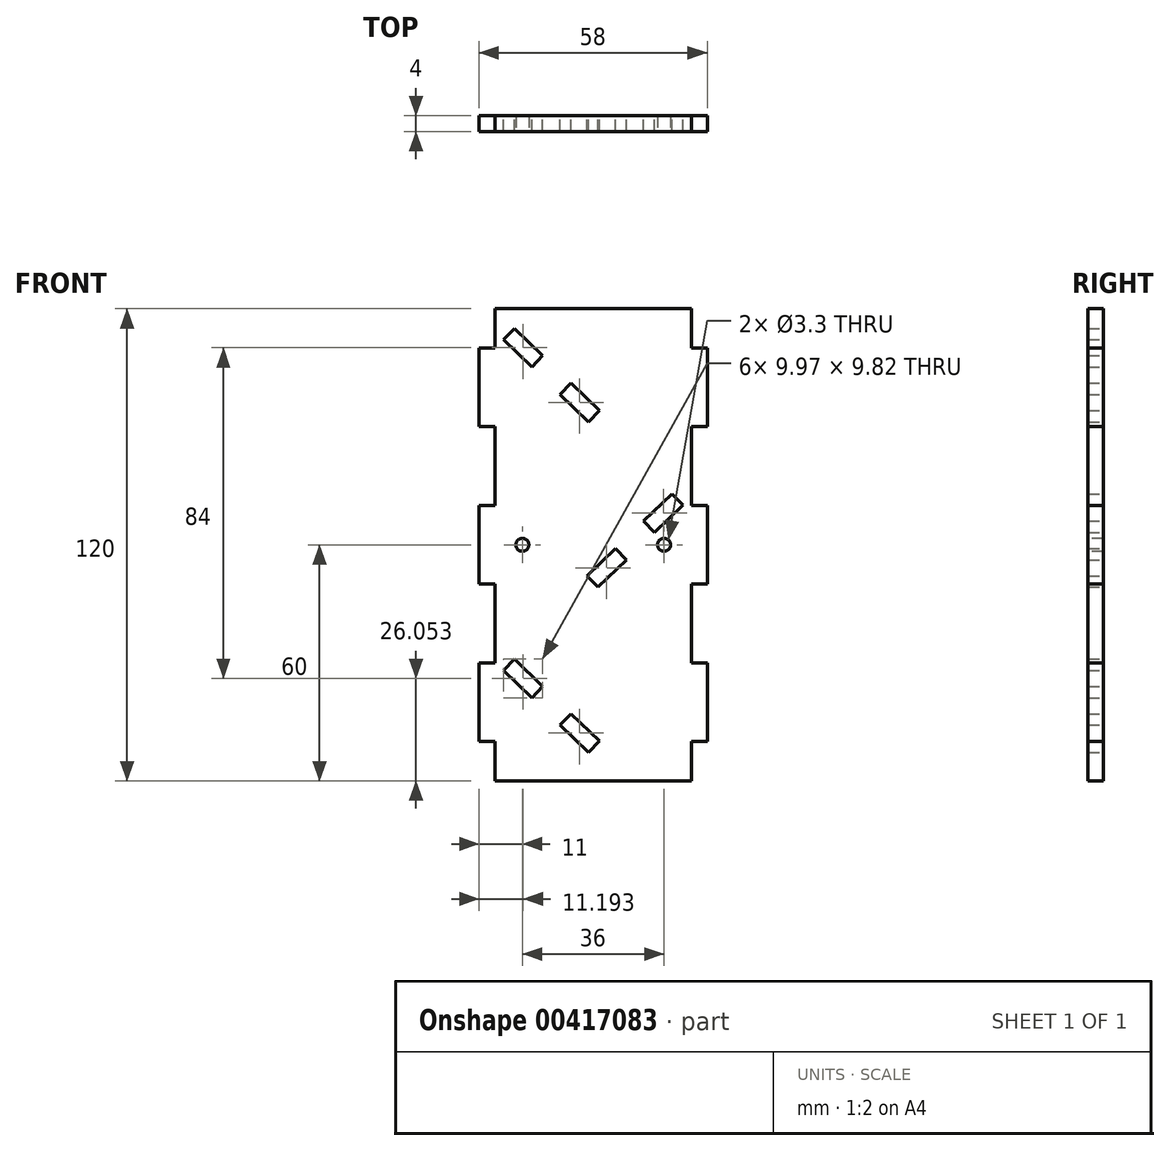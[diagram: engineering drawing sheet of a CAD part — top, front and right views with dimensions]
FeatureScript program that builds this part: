
annotation { "Feature Type Name" : "Feature", "Feature Type Description" : "" }
export const myFeature = defineFeature(function(context is Context, id is Id, definition is map)
    precondition{}
    {
        {
            var Q0;
            Q0=qCreatedBy(makeId("Front.planeOp"),FACE);
            var sketch = newSketch(context, id + "F0", { "sketchPlane" : qUnion([Q0])});
            skLineSegment(sketch, "E0.bottom", {"start": v(25, -60) * mm, "end": v(-25, -60) * mm});
            skLineSegment(sketch, "E0.top", {"start": v(25, 60) * mm, "end": v(-25, 60) * mm});
            skLineSegment(sketch, "E0.left", {"start": v(25, -60) * mm, "end": v(25, 60) * mm});
            skLineSegment(sketch, "E0.right", {"start": v(-25, -60) * mm, "end": v(-25, 60) * mm});
            skPoint(sketch, "E0.middle", {"position": v(0, 0) * mm});
            skLineSegment(sketch, "E1", {"start": v(-25, 57) * mm, "end": v(3.77, 29.21) * mm, "construction": true});
            skLineSegment(sketch, "E2", {"start": v(25, 15.2) * mm, "end": v(-2.79, -13.57) * mm, "construction": true});
            skLineSegment(sketch, "E3", {"start": v(-25, -27.04) * mm, "end": v(4.25, -54.32) * mm, "construction": true});
            skLineSegment(sketch, "E4", {"start": v(-21.4, 53.53) * mm, "end": v(-20.01, 54.97) * mm});
            skLineSegment(sketch, "E5", {"start": v(-20.01, 54.97) * mm, "end": v(-12.82, 48.02) * mm});
            skLineSegment(sketch, "E6", {"start": v(-12.82, 48.02) * mm, "end": v(-14.2, 46.58) * mm});
            skLineSegment(sketch, "E7", {"start": v(-7.02, 39.63) * mm, "end": v(-5.63, 41.07) * mm});
            skLineSegment(sketch, "E8", {"start": v(-5.63, 41.07) * mm, "end": v(1.57, 34.13) * mm});
            skLineSegment(sketch, "E9", {"start": v(1.57, 34.13) * mm, "end": v(0.18, 32.69) * mm});
            skLineSegment(sketch, "E10.MirrorCS", {"start": v(-21.4, 53.53) * mm, "end": v(-22.8, 52.09) * mm});
            skLineSegment(sketch, "E11.MirrorCS", {"start": v(-22.8, 52.09) * mm, "end": v(-15.6, 45.14) * mm});
            skLineSegment(sketch, "E12.MirrorCS", {"start": v(-15.6, 45.14) * mm, "end": v(-14.2, 46.58) * mm});
            skLineSegment(sketch, "E13.MirrorCS", {"start": v(-7.02, 39.63) * mm, "end": v(-8.4, 38.2) * mm});
            skLineSegment(sketch, "E14.MirrorCS", {"start": v(-8.4, 38.2) * mm, "end": v(-1.21, 31.25) * mm});
            skLineSegment(sketch, "E15.MirrorCS", {"start": v(-1.21, 31.25) * mm, "end": v(0.18, 32.69) * mm});
            skLineSegment(sketch, "E16.0.1.0", {"start": v(-8.4, -3.8) * mm, "end": v(-1.21, -10.75) * mm, "construction": true});
            skLineSegment(sketch, "E16.0.1.1", {"start": v(-20.01, 12.97) * mm, "end": v(-12.82, 6.02) * mm, "construction": true});
            skLineSegment(sketch, "E16.0.1.2", {"start": v(-5.63, -0.93) * mm, "end": v(1.57, -7.87) * mm, "construction": true});
            skLineSegment(sketch, "E16.0.1.3", {"start": v(-22.8, 10.09) * mm, "end": v(-15.6, 3.14) * mm, "construction": true});
            skLineSegment(sketch, "E16.0.1.4", {"start": v(-12.82, 6.02) * mm, "end": v(-14.2, 4.58) * mm, "construction": true});
            skLineSegment(sketch, "E16.0.1.5", {"start": v(-7.02, -2.37) * mm, "end": v(-5.63, -0.93) * mm, "construction": true});
            skLineSegment(sketch, "E16.0.1.6", {"start": v(-21.4, 11.53) * mm, "end": v(-20.01, 12.97) * mm, "construction": true});
            skLineSegment(sketch, "E16.0.1.7", {"start": v(-21.4, 11.53) * mm, "end": v(-22.8, 10.09) * mm, "construction": true});
            skLineSegment(sketch, "E16.0.1.8", {"start": v(1.57, -7.87) * mm, "end": v(0.18, -9.31) * mm, "construction": true});
            skLineSegment(sketch, "E16.0.1.9", {"start": v(-15.6, 3.14) * mm, "end": v(-14.2, 4.58) * mm, "construction": true});
            skLineSegment(sketch, "E16.0.1.10", {"start": v(-1.21, -10.75) * mm, "end": v(0.18, -9.31) * mm, "construction": true});
            skLineSegment(sketch, "E16.0.1.11", {"start": v(-7.02, -2.37) * mm, "end": v(-8.4, -3.8) * mm, "construction": true});
            skLineSegment(sketch, "E16.direction1", {"start": v(-22.8, 52.09) * mm, "end": v(2.55, 52.09) * mm, "construction": true});
            skLineSegment(sketch, "E16.direction2", {"start": v(-22.8, 52.09) * mm, "end": v(-22.8, 10.09) * mm, "construction": true});
            skLineSegment(sketch, "E17.0.0.2", {"start": v(-8.4, -45.8) * mm, "end": v(-1.21, -52.75) * mm});
            skLineSegment(sketch, "E17.3.0.2", {"start": v(-20.01, -29.03) * mm, "end": v(-12.82, -35.98) * mm});
            skLineSegment(sketch, "E17.6.0.2", {"start": v(-5.63, -42.93) * mm, "end": v(1.57, -49.87) * mm});
            skLineSegment(sketch, "E17.9.0.2", {"start": v(-22.8, -31.91) * mm, "end": v(-15.6, -38.86) * mm});
            skLineSegment(sketch, "E17.12.0.2", {"start": v(-12.82, -35.98) * mm, "end": v(-14.2, -37.42) * mm});
            skLineSegment(sketch, "E17.15.0.2", {"start": v(-7.02, -44.37) * mm, "end": v(-5.63, -42.93) * mm});
            skLineSegment(sketch, "E17.18.0.2", {"start": v(-21.4, -30.47) * mm, "end": v(-20.01, -29.03) * mm});
            skLineSegment(sketch, "E17.21.0.2", {"start": v(-21.4, -30.47) * mm, "end": v(-22.8, -31.91) * mm});
            skLineSegment(sketch, "E17.24.0.2", {"start": v(1.57, -49.87) * mm, "end": v(0.18, -51.31) * mm});
            skLineSegment(sketch, "E17.27.0.2", {"start": v(-15.6, -38.86) * mm, "end": v(-14.2, -37.42) * mm});
            skLineSegment(sketch, "E17.30.0.2", {"start": v(-1.21, -52.75) * mm, "end": v(0.18, -51.31) * mm});
            skLineSegment(sketch, "E17.33.0.2", {"start": v(-7.02, -44.37) * mm, "end": v(-8.4, -45.8) * mm});
            skLineSegment(sketch, "E18.MirrorCS", {"start": v(21.4, 11.53) * mm, "end": v(22.8, 10.09) * mm});
            skLineSegment(sketch, "E19.MirrorCS", {"start": v(21.4, 11.53) * mm, "end": v(20.01, 12.97) * mm});
            skLineSegment(sketch, "E20.MirrorCS", {"start": v(7.02, -2.37) * mm, "end": v(8.4, -3.8) * mm});
            skLineSegment(sketch, "E21.MirrorCS", {"start": v(15.6, 3.14) * mm, "end": v(14.2, 4.58) * mm});
            skLineSegment(sketch, "E22.MirrorCS", {"start": v(12.82, 6.02) * mm, "end": v(14.2, 4.58) * mm});
            skLineSegment(sketch, "E23.MirrorCS", {"start": v(7.02, -2.37) * mm, "end": v(5.63, -0.93) * mm});
            skLineSegment(sketch, "E24.MirrorCS", {"start": v(-1.57, -7.87) * mm, "end": v(-0.18, -9.31) * mm});
            skLineSegment(sketch, "E25.MirrorCS", {"start": v(1.21, -10.75) * mm, "end": v(-0.18, -9.31) * mm});
            skLineSegment(sketch, "E26.MirrorCS", {"start": v(22.8, 10.09) * mm, "end": v(15.6, 3.14) * mm});
            skLineSegment(sketch, "E27.MirrorCS", {"start": v(8.4, -3.8) * mm, "end": v(1.21, -10.75) * mm});
            skLineSegment(sketch, "E28.MirrorCS", {"start": v(20.01, 12.97) * mm, "end": v(12.82, 6.02) * mm});
            skLineSegment(sketch, "E29.MirrorCS", {"start": v(5.63, -0.93) * mm, "end": v(-1.57, -7.87) * mm});
            skSolve(sketch);
        }
        {
            var Q0;
            Q0=makeQuery(id+"F0.imprint","IMPRINT",FACE,{"disambiguationData":[TD([[makeQuery(id+"F0.imprint","IMPRINT",EDGE,{"derivedFrom":sQuery(id+"F0.wireOp",EDGE,"E0.bottom")}),-1.0]])]});
            extrude(context, id + "F1", {"entities" : qUnion([Q0]), "depth" : 4 * mm});
        }
        {
            var Q0;
            Q0=makeQuery(id+"F1.opExtrude","CAP_FACE",FACE,{"disambiguationData":[OSD([sQuery(id+"F0.wireOp",EDGE,"E0.bottom"),sQuery(id+"F0.wireOp",EDGE,"E0.top"),sQuery(id+"F0.wireOp",EDGE,"E0.left"),sQuery(id+"F0.wireOp",EDGE,"E0.right"),sQuery(id+"F0.wireOp",EDGE,"E4"),sQuery(id+"F0.wireOp",EDGE,"E5"),sQuery(id+"F0.wireOp",EDGE,"E6"),sQuery(id+"F0.wireOp",EDGE,"E7"),sQuery(id+"F0.wireOp",EDGE,"E8"),sQuery(id+"F0.wireOp",EDGE,"E9"),sQuery(id+"F0.wireOp",EDGE,"E10.MirrorCS"),sQuery(id+"F0.wireOp",EDGE,"E11.MirrorCS"),sQuery(id+"F0.wireOp",EDGE,"E12.MirrorCS"),sQuery(id+"F0.wireOp",EDGE,"E13.MirrorCS"),sQuery(id+"F0.wireOp",EDGE,"E14.MirrorCS"),sQuery(id+"F0.wireOp",EDGE,"E15.MirrorCS"),sQuery(id+"F0.wireOp",EDGE,"E17.0.0.2"),sQuery(id+"F0.wireOp",EDGE,"E17.3.0.2"),sQuery(id+"F0.wireOp",EDGE,"E17.6.0.2"),sQuery(id+"F0.wireOp",EDGE,"E17.9.0.2"),sQuery(id+"F0.wireOp",EDGE,"E17.12.0.2"),sQuery(id+"F0.wireOp",EDGE,"E17.15.0.2"),sQuery(id+"F0.wireOp",EDGE,"E17.18.0.2"),sQuery(id+"F0.wireOp",EDGE,"E17.21.0.2"),sQuery(id+"F0.wireOp",EDGE,"E17.24.0.2"),sQuery(id+"F0.wireOp",EDGE,"E17.27.0.2"),sQuery(id+"F0.wireOp",EDGE,"E17.30.0.2"),sQuery(id+"F0.wireOp",EDGE,"E17.33.0.2"),sQuery(id+"F0.wireOp",EDGE,"E18.MirrorCS"),sQuery(id+"F0.wireOp",EDGE,"E19.MirrorCS"),sQuery(id+"F0.wireOp",EDGE,"E20.MirrorCS"),sQuery(id+"F0.wireOp",EDGE,"E21.MirrorCS"),sQuery(id+"F0.wireOp",EDGE,"E22.MirrorCS"),sQuery(id+"F0.wireOp",EDGE,"E23.MirrorCS"),sQuery(id+"F0.wireOp",EDGE,"E24.MirrorCS"),sQuery(id+"F0.wireOp",EDGE,"E25.MirrorCS"),sQuery(id+"F0.wireOp",EDGE,"E26.MirrorCS"),sQuery(id+"F0.wireOp",EDGE,"E27.MirrorCS"),sQuery(id+"F0.wireOp",EDGE,"E28.MirrorCS"),sQuery(id+"F0.wireOp",EDGE,"E29.MirrorCS")])],"isStart":false});
            var sketch = newSketch(context, id + "F2", { "sketchPlane" : qUnion([Q0])});
            skLineSegment(sketch, "E30.bottom", {"start": v(-25, 50) * mm, "end": v(-29, 50) * mm});
            skLineSegment(sketch, "E30.top", {"start": v(-25, 30) * mm, "end": v(-29, 30) * mm});
            skLineSegment(sketch, "E30.left", {"start": v(-25, 50) * mm, "end": v(-25, 30) * mm});
            skLineSegment(sketch, "E30.right", {"start": v(-29, 50) * mm, "end": v(-29, 30) * mm});
            skLineSegment(sketch, "E31.bottom", {"start": v(-25, 0) * mm, "end": v(-29, 0) * mm});
            skLineSegment(sketch, "E31.top", {"start": v(-25, 10) * mm, "end": v(-29, 10) * mm});
            skLineSegment(sketch, "E31.left", {"start": v(-25, 0) * mm, "end": v(-25, 10) * mm});
            skLineSegment(sketch, "E31.right", {"start": v(-29, 0) * mm, "end": v(-29, 10) * mm});
            skLineSegment(sketch, "E32.MirrorCS", {"start": v(-25, -10) * mm, "end": v(-29, -10) * mm});
            skLineSegment(sketch, "E33.MirrorCS", {"start": v(-25, -30) * mm, "end": v(-29, -30) * mm});
            skLineSegment(sketch, "E34.MirrorCS", {"start": v(-25, -50) * mm, "end": v(-29, -50) * mm});
            skLineSegment(sketch, "E35.MirrorCS", {"start": v(-25, 0) * mm, "end": v(-25, -10) * mm});
            skLineSegment(sketch, "E36.MirrorCS", {"start": v(-29, -50) * mm, "end": v(-29, -30) * mm});
            skLineSegment(sketch, "E37.MirrorCS", {"start": v(-25, -50) * mm, "end": v(-25, -30) * mm});
            skLineSegment(sketch, "E38.MirrorCS", {"start": v(-29, 0) * mm, "end": v(-29, -10) * mm});
            skLineSegment(sketch, "E39.MirrorCS", {"start": v(25, 0) * mm, "end": v(29, 0) * mm});
            skLineSegment(sketch, "E40.MirrorCS", {"start": v(25, 10) * mm, "end": v(29, 10) * mm});
            skLineSegment(sketch, "E41.MirrorCS", {"start": v(25, 30) * mm, "end": v(29, 30) * mm});
            skLineSegment(sketch, "E42.MirrorCS", {"start": v(25, 50) * mm, "end": v(29, 50) * mm});
            skLineSegment(sketch, "E43.MirrorCS", {"start": v(25, -10) * mm, "end": v(29, -10) * mm});
            skLineSegment(sketch, "E44.MirrorCS", {"start": v(25, -30) * mm, "end": v(29, -30) * mm});
            skLineSegment(sketch, "E45.MirrorCS", {"start": v(25, -50) * mm, "end": v(29, -50) * mm});
            skLineSegment(sketch, "E46.MirrorCS", {"start": v(25, 0) * mm, "end": v(25, 10) * mm});
            skLineSegment(sketch, "E47.MirrorCS", {"start": v(29, 50) * mm, "end": v(29, 30) * mm});
            skLineSegment(sketch, "E48.MirrorCS", {"start": v(25, 50) * mm, "end": v(25, 30) * mm});
            skLineSegment(sketch, "E49.MirrorCS", {"start": v(29, 0) * mm, "end": v(29, -10) * mm});
            skLineSegment(sketch, "E50.MirrorCS", {"start": v(25, -50) * mm, "end": v(25, -30) * mm});
            skLineSegment(sketch, "E51.MirrorCS", {"start": v(29, -50) * mm, "end": v(29, -30) * mm});
            skLineSegment(sketch, "E52.MirrorCS", {"start": v(29, 0) * mm, "end": v(29, 10) * mm});
            skLineSegment(sketch, "E53.MirrorCS", {"start": v(25, 0) * mm, "end": v(25, -10) * mm});
            skSolve(sketch);
        }
        {
            var Q0;
            Q0 = qSketchRegion(id + "F2", true);
            extrude(context, id + "F3", {"entities" : qUnion([Q0]), "operationType" : NewBodyOperationType.ADD, "oppositeDirection" : true, "depth" : 4 * mm});
        }
        {
            var Q0;
            Q0=makeQuery(id+"F3.boolean.opBoolean","MERGE",FACE,{"derivedFrom":[makeQuery(id+"F1.opExtrude","CAP_FACE",FACE,{"disambiguationData":[OSD([sQuery(id+"F0.wireOp",EDGE,"E0.bottom"),sQuery(id+"F0.wireOp",EDGE,"E0.top"),sQuery(id+"F0.wireOp",EDGE,"E0.left"),sQuery(id+"F0.wireOp",EDGE,"E0.right"),sQuery(id+"F0.wireOp",EDGE,"E4"),sQuery(id+"F0.wireOp",EDGE,"E5"),sQuery(id+"F0.wireOp",EDGE,"E6"),sQuery(id+"F0.wireOp",EDGE,"E7"),sQuery(id+"F0.wireOp",EDGE,"E8"),sQuery(id+"F0.wireOp",EDGE,"E9"),sQuery(id+"F0.wireOp",EDGE,"E10.MirrorCS"),sQuery(id+"F0.wireOp",EDGE,"E11.MirrorCS"),sQuery(id+"F0.wireOp",EDGE,"E12.MirrorCS"),sQuery(id+"F0.wireOp",EDGE,"E13.MirrorCS"),sQuery(id+"F0.wireOp",EDGE,"E14.MirrorCS"),sQuery(id+"F0.wireOp",EDGE,"E15.MirrorCS"),sQuery(id+"F0.wireOp",EDGE,"E17.0.0.2"),sQuery(id+"F0.wireOp",EDGE,"E17.3.0.2"),sQuery(id+"F0.wireOp",EDGE,"E17.6.0.2"),sQuery(id+"F0.wireOp",EDGE,"E17.9.0.2"),sQuery(id+"F0.wireOp",EDGE,"E17.12.0.2"),sQuery(id+"F0.wireOp",EDGE,"E17.15.0.2"),sQuery(id+"F0.wireOp",EDGE,"E17.18.0.2"),sQuery(id+"F0.wireOp",EDGE,"E17.21.0.2"),sQuery(id+"F0.wireOp",EDGE,"E17.24.0.2"),sQuery(id+"F0.wireOp",EDGE,"E17.27.0.2"),sQuery(id+"F0.wireOp",EDGE,"E17.30.0.2"),sQuery(id+"F0.wireOp",EDGE,"E17.33.0.2"),sQuery(id+"F0.wireOp",EDGE,"E18.MirrorCS"),sQuery(id+"F0.wireOp",EDGE,"E19.MirrorCS"),sQuery(id+"F0.wireOp",EDGE,"E20.MirrorCS"),sQuery(id+"F0.wireOp",EDGE,"E21.MirrorCS"),sQuery(id+"F0.wireOp",EDGE,"E22.MirrorCS"),sQuery(id+"F0.wireOp",EDGE,"E23.MirrorCS"),sQuery(id+"F0.wireOp",EDGE,"E24.MirrorCS"),sQuery(id+"F0.wireOp",EDGE,"E25.MirrorCS"),sQuery(id+"F0.wireOp",EDGE,"E26.MirrorCS"),sQuery(id+"F0.wireOp",EDGE,"E27.MirrorCS"),sQuery(id+"F0.wireOp",EDGE,"E28.MirrorCS"),sQuery(id+"F0.wireOp",EDGE,"E29.MirrorCS")])],"isStart":false}),makeQuery(id+"F3.opExtrude","CAP_FACE",FACE,{"disambiguationData":[OSD([sQuery(id+"F2.wireOp",EDGE,"E30.bottom"),sQuery(id+"F2.wireOp",EDGE,"E30.top"),sQuery(id+"F2.wireOp",EDGE,"E30.left"),sQuery(id+"F2.wireOp",EDGE,"E30.right")])],"isStart":true}),makeQuery(id+"F3.opExtrude","CAP_FACE",FACE,{"disambiguationData":[OSD([sQuery(id+"F2.wireOp",EDGE,"E31.top"),sQuery(id+"F2.wireOp",EDGE,"E31.left"),sQuery(id+"F2.wireOp",EDGE,"E31.right"),sQuery(id+"F2.wireOp",EDGE,"E32.MirrorCS"),sQuery(id+"F2.wireOp",EDGE,"E35.MirrorCS"),sQuery(id+"F2.wireOp",EDGE,"E38.MirrorCS")])],"isStart":true}),makeQuery(id+"F3.opExtrude","CAP_FACE",FACE,{"disambiguationData":[OSD([sQuery(id+"F2.wireOp",EDGE,"E33.MirrorCS"),sQuery(id+"F2.wireOp",EDGE,"E34.MirrorCS"),sQuery(id+"F2.wireOp",EDGE,"E36.MirrorCS"),sQuery(id+"F2.wireOp",EDGE,"E37.MirrorCS")])],"isStart":true}),makeQuery(id+"F3.opExtrude","CAP_FACE",FACE,{"disambiguationData":[OSD([sQuery(id+"F2.wireOp",EDGE,"E40.MirrorCS"),sQuery(id+"F2.wireOp",EDGE,"E43.MirrorCS"),sQuery(id+"F2.wireOp",EDGE,"E46.MirrorCS"),sQuery(id+"F2.wireOp",EDGE,"E49.MirrorCS"),sQuery(id+"F2.wireOp",EDGE,"E52.MirrorCS"),sQuery(id+"F2.wireOp",EDGE,"E53.MirrorCS")])],"isStart":true}),makeQuery(id+"F3.opExtrude","CAP_FACE",FACE,{"disambiguationData":[OSD([sQuery(id+"F2.wireOp",EDGE,"E41.MirrorCS"),sQuery(id+"F2.wireOp",EDGE,"E42.MirrorCS"),sQuery(id+"F2.wireOp",EDGE,"E47.MirrorCS"),sQuery(id+"F2.wireOp",EDGE,"E48.MirrorCS")])],"isStart":true}),makeQuery(id+"F3.opExtrude","CAP_FACE",FACE,{"disambiguationData":[OSD([sQuery(id+"F2.wireOp",EDGE,"E44.MirrorCS"),sQuery(id+"F2.wireOp",EDGE,"E45.MirrorCS"),sQuery(id+"F2.wireOp",EDGE,"E50.MirrorCS"),sQuery(id+"F2.wireOp",EDGE,"E51.MirrorCS")])],"isStart":true})]});
            var sketch = newSketch(context, id + "F4", { "sketchPlane" : qUnion([Q0])});
            skPoint(sketch, "E54", {"position": v(-18, 0) * mm});
            skPoint(sketch, "E55.MirrorP", {"position": v(18, 0) * mm});
            skSolve(sketch);
        }
        {
            var Q0;
            Q0=sQuery(id+"F4.wireOp",VERTEX,"E54");
            var Q1;
            Q1=sQuery(id+"F4.wireOp",VERTEX,"E55.MirrorP");
            var Q2;
            Q2=makeQuery(id+"F1.opExtrude","SWEPT_BODY",BODY,{"disambiguationData":[OSD([sQuery(id+"F0.wireOp",EDGE,"E0.bottom"),sQuery(id+"F0.wireOp",EDGE,"E0.top"),sQuery(id+"F0.wireOp",EDGE,"E0.left"),sQuery(id+"F0.wireOp",EDGE,"E0.right"),sQuery(id+"F0.wireOp",EDGE,"E4"),sQuery(id+"F0.wireOp",EDGE,"E5"),sQuery(id+"F0.wireOp",EDGE,"E6"),sQuery(id+"F0.wireOp",EDGE,"E7"),sQuery(id+"F0.wireOp",EDGE,"E8"),sQuery(id+"F0.wireOp",EDGE,"E9"),sQuery(id+"F0.wireOp",EDGE,"E10.MirrorCS"),sQuery(id+"F0.wireOp",EDGE,"E11.MirrorCS"),sQuery(id+"F0.wireOp",EDGE,"E12.MirrorCS"),sQuery(id+"F0.wireOp",EDGE,"E13.MirrorCS"),sQuery(id+"F0.wireOp",EDGE,"E14.MirrorCS"),sQuery(id+"F0.wireOp",EDGE,"E15.MirrorCS"),sQuery(id+"F0.wireOp",EDGE,"E17.0.0.2"),sQuery(id+"F0.wireOp",EDGE,"E17.3.0.2"),sQuery(id+"F0.wireOp",EDGE,"E17.6.0.2"),sQuery(id+"F0.wireOp",EDGE,"E17.9.0.2"),sQuery(id+"F0.wireOp",EDGE,"E17.12.0.2"),sQuery(id+"F0.wireOp",EDGE,"E17.15.0.2"),sQuery(id+"F0.wireOp",EDGE,"E17.18.0.2"),sQuery(id+"F0.wireOp",EDGE,"E17.21.0.2"),sQuery(id+"F0.wireOp",EDGE,"E17.24.0.2"),sQuery(id+"F0.wireOp",EDGE,"E17.27.0.2"),sQuery(id+"F0.wireOp",EDGE,"E17.30.0.2"),sQuery(id+"F0.wireOp",EDGE,"E17.33.0.2"),sQuery(id+"F0.wireOp",EDGE,"E18.MirrorCS"),sQuery(id+"F0.wireOp",EDGE,"E19.MirrorCS"),sQuery(id+"F0.wireOp",EDGE,"E20.MirrorCS"),sQuery(id+"F0.wireOp",EDGE,"E21.MirrorCS"),sQuery(id+"F0.wireOp",EDGE,"E22.MirrorCS"),sQuery(id+"F0.wireOp",EDGE,"E23.MirrorCS"),sQuery(id+"F0.wireOp",EDGE,"E24.MirrorCS"),sQuery(id+"F0.wireOp",EDGE,"E25.MirrorCS"),sQuery(id+"F0.wireOp",EDGE,"E26.MirrorCS"),sQuery(id+"F0.wireOp",EDGE,"E27.MirrorCS"),sQuery(id+"F0.wireOp",EDGE,"E28.MirrorCS"),sQuery(id+"F0.wireOp",EDGE,"E29.MirrorCS")])]});
            hole(context, id + "F5", {"style" : HoleStyle.SIMPLE, "endStyle" : HoleEndStyle.THROUGH, "standardTappedOrClearance" : lookupTablePath({ "standard" : "ISO", "fit" : "Normal", "size" : "M3", "type" : "Clearance" }), "standardBlindInLast" : lookupTablePath({ "fit" : "Standard", "standard" : "ISO", "size" : "M3", "type" : "Clearance" }), "holeDiameter" : 3.3 * mm, "isTappedThrough" : true, "tappedDepth" : 12 * mm, "tapClearance" : 3, "startFromSketch" : true, "locations" : qUnion([Q0, Q1]), "scope" : qUnion([Q2])});
        }
    });
